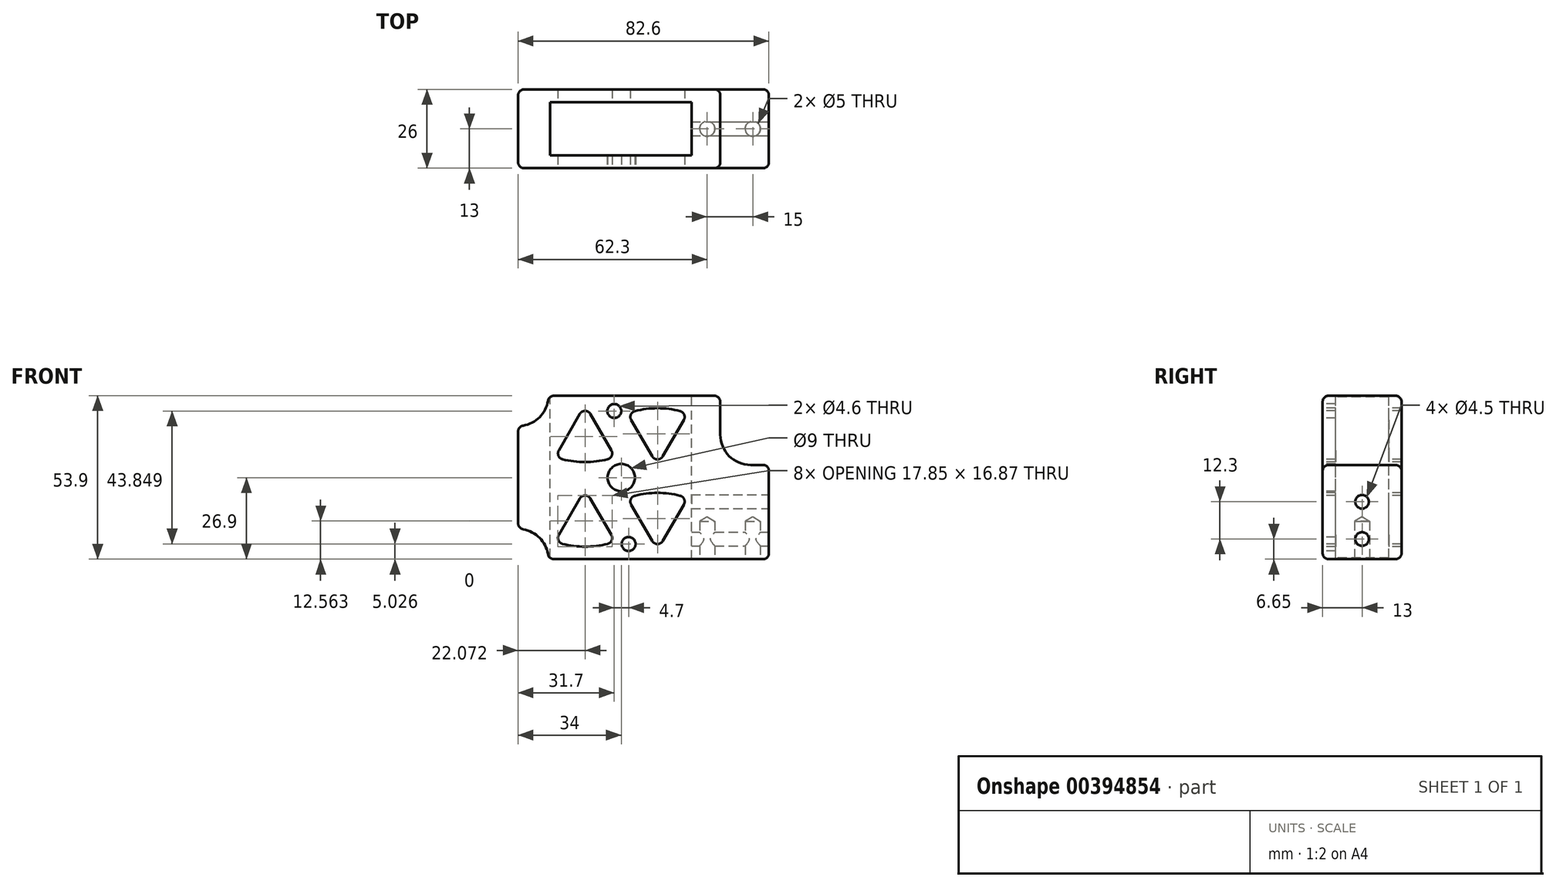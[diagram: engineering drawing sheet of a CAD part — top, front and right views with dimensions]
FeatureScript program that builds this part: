
annotation { "Feature Type Name" : "Feature", "Feature Type Description" : "" }
export const myFeature = defineFeature(function(context is Context, id is Id, definition is map)
    precondition{}
    {
        {
            var Q0;
            Q0=qCreatedBy(makeId("Front.planeOp"),FACE);
            var sketch = newSketch(context, id + "F0", { "sketchPlane" : qUnion([Q0])});
            skLineSegment(sketch, "E0.bottom", {"start": v(-29.47, 53.9) * mm, "end": v(23.3, 53.9) * mm});
            skLineSegment(sketch, "E0.top", {"start": v(-29.47, 0) * mm, "end": v(39.3, 0) * mm});
            skLineSegment(sketch, "E0.left", {"start": v(-41.3, 42.07) * mm, "end": v(-41.3, 11.83) * mm});
            skLineSegment(sketch, "E0.right", {"start": v(41.3, 29.08) * mm, "end": v(41.3, 2) * mm});
            skArc(sketch, "E1", {"start": v(-31.44, 1.67) * mm, "mid": v(-34.23, 7.07) * mm, "end": v(-39.63, 9.86) * mm});
            skArc(sketch, "E2", {"start": v(-39.63, 44.04) * mm, "mid": v(-34.23, 46.83) * mm, "end": v(-31.44, 52.23) * mm});
            skLineSegment(sketch, "E3", {"start": v(25.3, 51.9) * mm, "end": v(25.3, 41.08) * mm});
            skLineSegment(sketch, "E4", {"start": v(35.3, 31.08) * mm, "end": v(39.3, 31.08) * mm});
            skArc(sketch, "E5", {"start": v(25.3, 41.08) * mm, "mid": v(28.23, 34) * mm, "end": v(35.3, 31.08) * mm});
            skPoint(sketch, "E6.visualSharp", {"position": v(-31.3, 53.9) * mm});
            skArc(sketch, "E6.filletArc", {"start": v(-29.47, 53.9) * mm, "mid": v(-30.76, 53.43) * mm, "end": v(-31.44, 52.23) * mm});
            skPoint(sketch, "E7.visualSharp", {"position": v(-41.3, 43.9) * mm});
            skArc(sketch, "E7.filletArc", {"start": v(-39.63, 44.04) * mm, "mid": v(-40.83, 43.36) * mm, "end": v(-41.3, 42.07) * mm});
            skPoint(sketch, "E8.visualSharp", {"position": v(-41.3, 10) * mm});
            skArc(sketch, "E8.filletArc", {"start": v(-41.3, 11.83) * mm, "mid": v(-40.83, 10.54) * mm, "end": v(-39.63, 9.86) * mm});
            skPoint(sketch, "E9.visualSharp", {"position": v(-31.3, 0) * mm});
            skArc(sketch, "E9.filletArc", {"start": v(-31.44, 1.67) * mm, "mid": v(-30.76, 0.47) * mm, "end": v(-29.47, 0) * mm});
            skPoint(sketch, "E10.visualSharp", {"position": v(41.3, 0) * mm});
            skArc(sketch, "E10.filletArc", {"start": v(39.3, 0) * mm, "mid": v(40.71, 0.59) * mm, "end": v(41.3, 2) * mm});
            skPoint(sketch, "E11.orphan", {"position": v(41.3, 53.9) * mm});
            skPoint(sketch, "E12.visualSharp", {"position": v(25.3, 53.9) * mm});
            skArc(sketch, "E12.filletArc", {"start": v(25.3, 51.9) * mm, "mid": v(24.71, 53.31) * mm, "end": v(23.3, 53.9) * mm});
            skPoint(sketch, "E13.visualSharp", {"position": v(41.3, 31.08) * mm});
            skArc(sketch, "E13.filletArc", {"start": v(41.3, 29.08) * mm, "mid": v(40.71, 30.5) * mm, "end": v(39.3, 31.08) * mm});
            skSolve(sketch);
        }
        {
            var Q0;
            Q0=qSketchRegion(id+"F0",true);
            extrude(context, id + "F1", {"entities" : qUnion([Q0]), "oppositeDirection" : true, "depth" : 26 * mm});
        }
        {
            var Q0;
            Q0=makeQuery(id+"F1.opExtrude","SWEPT_FACE",FACE,{"disambiguationData":[OSD([sQuery(id+"F0.wireOp",EDGE,"E0.bottom")])]});
            var sketch = newSketch(context, id + "F2", { "sketchPlane" : qUnion([Q0])});
            skLineSegment(sketch, "E14.bottom", {"start": v(-30.72, 21.75) * mm, "end": v(15.8, 21.75) * mm});
            skLineSegment(sketch, "E14.top", {"start": v(-30.72, 4.25) * mm, "end": v(15.8, 4.25) * mm});
            skLineSegment(sketch, "E14.left", {"start": v(-30.72, 21.75) * mm, "end": v(-30.72, 4.25) * mm});
            skLineSegment(sketch, "E14.right", {"start": v(15.8, 21.75) * mm, "end": v(15.8, 4.25) * mm});
            skSolve(sketch);
        }
        {
            var Q0;
            Q0=qSketchRegion(id+"F2",true);
            extrude(context, id + "F3", {"entities" : qUnion([Q0]), "operationType" : NewBodyOperationType.REMOVE, "endBound" : BoundingType.THROUGH_ALL, "oppositeDirection" : true, "depth" : 25 * mm});
        }
        {
            var Q0;
            Q0=makeQuery(id+"F1.opExtrude","CAP_FACE",FACE,{"disambiguationData":[OSD([sQuery(id+"F0.wireOp",EDGE,"E0.bottom"),sQuery(id+"F0.wireOp",EDGE,"E0.top"),sQuery(id+"F0.wireOp",EDGE,"E0.left"),sQuery(id+"F0.wireOp",EDGE,"E0.right"),sQuery(id+"F0.wireOp",EDGE,"E1"),sQuery(id+"F0.wireOp",EDGE,"E2"),sQuery(id+"F0.wireOp",EDGE,"E3"),sQuery(id+"F0.wireOp",EDGE,"E4"),sQuery(id+"F0.wireOp",EDGE,"E5"),sQuery(id+"F0.wireOp",EDGE,"E6.filletArc"),sQuery(id+"F0.wireOp",EDGE,"E7.filletArc"),sQuery(id+"F0.wireOp",EDGE,"E8.filletArc"),sQuery(id+"F0.wireOp",EDGE,"E9.filletArc"),sQuery(id+"F0.wireOp",EDGE,"E10.filletArc"),sQuery(id+"F0.wireOp",EDGE,"E12.filletArc"),sQuery(id+"F0.wireOp",EDGE,"E13.filletArc")])],"isStart":true});
            var sketch = newSketch(context, id + "F4", { "sketchPlane" : qUnion([Q0])});
            skPoint(sketch, "E15", {"position": v(-7.3, 26.9) * mm});
            skSolve(sketch);
        }
        {
            var Q0;
            Q0=sQuery(id+"F4.wireOp",VERTEX,"E15");
            var Q1;
            Q1=makeQuery(id+"F1.opExtrude","SWEPT_BODY",BODY,{"disambiguationData":[OSD([sQuery(id+"F0.wireOp",EDGE,"E0.bottom"),sQuery(id+"F0.wireOp",EDGE,"E0.top"),sQuery(id+"F0.wireOp",EDGE,"E0.left"),sQuery(id+"F0.wireOp",EDGE,"E0.right"),sQuery(id+"F0.wireOp",EDGE,"E1"),sQuery(id+"F0.wireOp",EDGE,"E2"),sQuery(id+"F0.wireOp",EDGE,"E3"),sQuery(id+"F0.wireOp",EDGE,"E4"),sQuery(id+"F0.wireOp",EDGE,"E5"),sQuery(id+"F0.wireOp",EDGE,"E6.filletArc"),sQuery(id+"F0.wireOp",EDGE,"E7.filletArc"),sQuery(id+"F0.wireOp",EDGE,"E8.filletArc"),sQuery(id+"F0.wireOp",EDGE,"E9.filletArc"),sQuery(id+"F0.wireOp",EDGE,"E10.filletArc"),sQuery(id+"F0.wireOp",EDGE,"E12.filletArc"),sQuery(id+"F0.wireOp",EDGE,"E13.filletArc")])]});
            hole(context, id + "F5", {"style" : HoleStyle.SIMPLE, "endStyle" : HoleEndStyle.BLIND, "holeDiameter" : 9 * mm, "holeDepth" : 12 * mm, "isTappedThrough" : true, "tappedDepth" : 12 * mm, "tapClearance" : 3, "locations" : qUnion([Q0]), "scope" : qUnion([Q1])});
        }
        {
            var Q0;
            Q0=makeQuery(id+"F1.opExtrude","SWEPT_FACE",FACE,{"disambiguationData":[OSD([sQuery(id+"F0.wireOp",EDGE,"E0.right")])]});
            var sketch = newSketch(context, id + "F6", { "sketchPlane" : qUnion([Q0])});
            skPoint(sketch, "E16", {"position": v(13, 18.95) * mm});
            skPoint(sketch, "E17", {"position": v(13, 6.65) * mm});
            skSolve(sketch);
        }
        {
            var Q0;
            Q0=sQuery(id+"F6.wireOp",VERTEX,"E16");
            var Q1;
            Q1=sQuery(id+"F6.wireOp",VERTEX,"E17");
            var Q2;
            Q2=makeQuery(id+"F1.opExtrude","SWEPT_BODY",BODY,{"disambiguationData":[OSD([sQuery(id+"F0.wireOp",EDGE,"E0.bottom"),sQuery(id+"F0.wireOp",EDGE,"E0.top"),sQuery(id+"F0.wireOp",EDGE,"E0.left"),sQuery(id+"F0.wireOp",EDGE,"E0.right"),sQuery(id+"F0.wireOp",EDGE,"E1"),sQuery(id+"F0.wireOp",EDGE,"E2"),sQuery(id+"F0.wireOp",EDGE,"E3"),sQuery(id+"F0.wireOp",EDGE,"E4"),sQuery(id+"F0.wireOp",EDGE,"E5"),sQuery(id+"F0.wireOp",EDGE,"E6.filletArc"),sQuery(id+"F0.wireOp",EDGE,"E7.filletArc"),sQuery(id+"F0.wireOp",EDGE,"E8.filletArc"),sQuery(id+"F0.wireOp",EDGE,"E9.filletArc"),sQuery(id+"F0.wireOp",EDGE,"E10.filletArc"),sQuery(id+"F0.wireOp",EDGE,"E12.filletArc"),sQuery(id+"F0.wireOp",EDGE,"E13.filletArc")])]});
            hole(context, id + "F7", {"style" : HoleStyle.SIMPLE, "endStyle" : HoleEndStyle.BLIND, "holeDiameter" : 4.5 * mm, "holeDepth" : 30 * mm, "isTappedThrough" : true, "tappedDepth" : 27.9 * mm, "tapClearance" : 3, "locations" : qUnion([Q0, Q1]), "scope" : qUnion([Q2])});
        }
        {
            var Q0;
            Q0=makeQuery(id+"F1.opExtrude","SWEPT_FACE",FACE,{"disambiguationData":[OSD([sQuery(id+"F0.wireOp",EDGE,"E0.top")])]});
            var sketch = newSketch(context, id + "F8", { "sketchPlane" : qUnion([Q0])});
            skPoint(sketch, "E18", {"position": v(36, -13) * mm});
            skPoint(sketch, "E18.positionSnap0", {"position": v(39.3, -13) * mm});
            skPoint(sketch, "E19", {"position": v(21, -13) * mm});
            skSolve(sketch);
        }
        {
            var Q0;
            Q0=sQuery(id+"F8.wireOp",VERTEX,"E18");
            var Q1;
            Q1=sQuery(id+"F8.wireOp",VERTEX,"E19");
            var Q2;
            Q2=makeQuery(id+"F1.opExtrude","SWEPT_BODY",BODY,{"disambiguationData":[OSD([sQuery(id+"F0.wireOp",EDGE,"E0.bottom"),sQuery(id+"F0.wireOp",EDGE,"E0.top"),sQuery(id+"F0.wireOp",EDGE,"E0.left"),sQuery(id+"F0.wireOp",EDGE,"E0.right"),sQuery(id+"F0.wireOp",EDGE,"E1"),sQuery(id+"F0.wireOp",EDGE,"E2"),sQuery(id+"F0.wireOp",EDGE,"E3"),sQuery(id+"F0.wireOp",EDGE,"E4"),sQuery(id+"F0.wireOp",EDGE,"E5"),sQuery(id+"F0.wireOp",EDGE,"E6.filletArc"),sQuery(id+"F0.wireOp",EDGE,"E7.filletArc"),sQuery(id+"F0.wireOp",EDGE,"E8.filletArc"),sQuery(id+"F0.wireOp",EDGE,"E9.filletArc"),sQuery(id+"F0.wireOp",EDGE,"E10.filletArc"),sQuery(id+"F0.wireOp",EDGE,"E12.filletArc"),sQuery(id+"F0.wireOp",EDGE,"E13.filletArc")])]});
            hole(context, id + "F9", {"style" : HoleStyle.SIMPLE, "endStyle" : HoleEndStyle.BLIND, "standardTappedOrClearance" : lookupTablePath({ "standard" : "ISO", "engagement" : "75%", "pitch" : "1 mm", "size" : "M6", "type" : "Tapped" }), "standardBlindInLast" : lookupTablePath({ "standard" : "ISO", "engagement" : "75%", "pitch" : "1 mm", "size" : "M6", "type" : "Tapped" }), "holeDiameter" : 5 * mm, "showTappedDepth" : true, "holeDepth" : 12.5 * mm, "isTappedThrough" : true, "tappedDepth" : 9.5 * mm, "tapClearance" : 3, "locations" : qUnion([Q0, Q1]), "scope" : qUnion([Q2]), "majorDiameter" : 6 * mm});
        }
        {
            var Q0;
            Q0=makeQuery(id+"F1.opExtrude","CAP_FACE",FACE,{"disambiguationData":[OSD([sQuery(id+"F0.wireOp",EDGE,"E0.bottom"),sQuery(id+"F0.wireOp",EDGE,"E0.top"),sQuery(id+"F0.wireOp",EDGE,"E0.left"),sQuery(id+"F0.wireOp",EDGE,"E0.right"),sQuery(id+"F0.wireOp",EDGE,"E1"),sQuery(id+"F0.wireOp",EDGE,"E2"),sQuery(id+"F0.wireOp",EDGE,"E3"),sQuery(id+"F0.wireOp",EDGE,"E4"),sQuery(id+"F0.wireOp",EDGE,"E5"),sQuery(id+"F0.wireOp",EDGE,"E6.filletArc"),sQuery(id+"F0.wireOp",EDGE,"E7.filletArc"),sQuery(id+"F0.wireOp",EDGE,"E8.filletArc"),sQuery(id+"F0.wireOp",EDGE,"E9.filletArc"),sQuery(id+"F0.wireOp",EDGE,"E10.filletArc"),sQuery(id+"F0.wireOp",EDGE,"E12.filletArc"),sQuery(id+"F0.wireOp",EDGE,"E13.filletArc")])],"isStart":true});
            var sketch = newSketch(context, id + "F10", { "sketchPlane" : qUnion([Q0])});
            skCircle(sketch, "E20", {"center": v(-9.6, 48.87) * mm, "radius": 2.3 * mm});
            skCircle(sketch, "E21", {"center": v(-4.9, 5.03) * mm, "radius": 2.3 * mm});
            skLineSegment(sketch, "E22", {"start": v(-66.21, 51.17) * mm, "end": v(48.12, 51.17) * mm, "construction": true});
            skLineSegment(sketch, "E23", {"start": v(-60.61, 2.73) * mm, "end": v(50.15, 2.73) * mm, "construction": true});
            skLineSegment(sketch, "E24", {"start": v(-9.6, 48.87) * mm, "end": v(-9.6, 53.9) * mm, "construction": true});
            skLineSegment(sketch, "E25", {"start": v(-4.9, 5.03) * mm, "end": v(-4.9, 0) * mm, "construction": true});
            skSolve(sketch);
        }
        {
            var Q0;
            Q0=sQuery(id+"F10.wireOp",VERTEX,"E20.center");
            var Q1;
            Q1=sQuery(id+"F10.wireOp",VERTEX,"E25.start");
            var Q2;
            Q2=makeQuery(id+"F1.opExtrude","SWEPT_BODY",BODY,{"disambiguationData":[OSD([sQuery(id+"F0.wireOp",EDGE,"E0.bottom"),sQuery(id+"F0.wireOp",EDGE,"E0.top"),sQuery(id+"F0.wireOp",EDGE,"E0.left"),sQuery(id+"F0.wireOp",EDGE,"E0.right"),sQuery(id+"F0.wireOp",EDGE,"E1"),sQuery(id+"F0.wireOp",EDGE,"E2"),sQuery(id+"F0.wireOp",EDGE,"E3"),sQuery(id+"F0.wireOp",EDGE,"E4"),sQuery(id+"F0.wireOp",EDGE,"E5"),sQuery(id+"F0.wireOp",EDGE,"E6.filletArc"),sQuery(id+"F0.wireOp",EDGE,"E7.filletArc"),sQuery(id+"F0.wireOp",EDGE,"E8.filletArc"),sQuery(id+"F0.wireOp",EDGE,"E9.filletArc"),sQuery(id+"F0.wireOp",EDGE,"E10.filletArc"),sQuery(id+"F0.wireOp",EDGE,"E12.filletArc"),sQuery(id+"F0.wireOp",EDGE,"E13.filletArc")])]});
            hole(context, id + "F11", {"style" : HoleStyle.SIMPLE, "endStyle" : HoleEndStyle.BLIND, "holeDiameter" : 4.6 * mm, "holeDepth" : 12.5 * mm, "isTappedThrough" : true, "tappedDepth" : 9.5 * mm, "tapClearance" : 3, "locations" : qUnion([Q0, Q1]), "scope" : qUnion([Q2])});
        }
        {
            var Q0;
            Q0=makeQuery(id+"F1.opExtrude","CAP_FACE",FACE,{"disambiguationData":[OSD([sQuery(id+"F0.wireOp",EDGE,"E0.bottom"),sQuery(id+"F0.wireOp",EDGE,"E0.top"),sQuery(id+"F0.wireOp",EDGE,"E0.left"),sQuery(id+"F0.wireOp",EDGE,"E0.right"),sQuery(id+"F0.wireOp",EDGE,"E1"),sQuery(id+"F0.wireOp",EDGE,"E2"),sQuery(id+"F0.wireOp",EDGE,"E3"),sQuery(id+"F0.wireOp",EDGE,"E4"),sQuery(id+"F0.wireOp",EDGE,"E5"),sQuery(id+"F0.wireOp",EDGE,"E6.filletArc"),sQuery(id+"F0.wireOp",EDGE,"E7.filletArc"),sQuery(id+"F0.wireOp",EDGE,"E8.filletArc"),sQuery(id+"F0.wireOp",EDGE,"E9.filletArc"),sQuery(id+"F0.wireOp",EDGE,"E10.filletArc"),sQuery(id+"F0.wireOp",EDGE,"E12.filletArc"),sQuery(id+"F0.wireOp",EDGE,"E13.filletArc")])],"isStart":true});
            var sketch = newSketch(context, id + "F12", { "sketchPlane" : qUnion([Q0])});
            skLineSegment(sketch, "E26", {"start": v(-17.5, 47.9) * mm, "end": v(-10.57, 35.9) * mm});
            skLineSegment(sketch, "E27", {"start": v(-12.3, 32.9) * mm, "end": v(-26.16, 32.9) * mm});
            skLineSegment(sketch, "E28", {"start": v(-27.89, 35.9) * mm, "end": v(-20.96, 47.9) * mm});
            skPoint(sketch, "E29.visualSharp", {"position": v(-19.23, 50.9) * mm});
            skArc(sketch, "E29.filletArc", {"start": v(-17.5, 47.9) * mm, "mid": v(-19.23, 48.9) * mm, "end": v(-20.96, 47.9) * mm});
            skArc(sketch, "E30.filletArc", {"start": v(-12.3, 32.9) * mm, "mid": v(-10.57, 33.9) * mm, "end": v(-10.57, 35.9) * mm});
            skPoint(sketch, "E31.visualSharp", {"position": v(-29.62, 32.9) * mm});
            skArc(sketch, "E31.filletArc", {"start": v(-27.89, 35.9) * mm, "mid": v(-27.89, 33.9) * mm, "end": v(-26.16, 32.9) * mm});
            skLineSegment(sketch, "E32", {"start": v(-7.3, 59.95) * mm, "end": v(-7.3, -3) * mm, "construction": true});
            skLineSegment(sketch, "E33", {"start": v(-48.51, 26.9) * mm, "end": v(45.71, 26.9) * mm, "construction": true});
            skLineSegment(sketch, "E34", {"start": v(-30.72, 56.6) * mm, "end": v(-30.72, -1.77) * mm, "construction": true});
            skLineSegment(sketch, "E35", {"start": v(-2.3, 48.9) * mm, "end": v(11.56, 48.9) * mm});
            skLineSegment(sketch, "E36", {"start": v(13.29, 45.9) * mm, "end": v(6.36, 33.9) * mm});
            skLineSegment(sketch, "E37", {"start": v(2.9, 33.9) * mm, "end": v(-4.03, 45.9) * mm});
            skPoint(sketch, "E38.visualSharp", {"position": v(4.63, 30.9) * mm});
            skArc(sketch, "E38.filletArc", {"start": v(2.9, 33.9) * mm, "mid": v(4.63, 32.9) * mm, "end": v(6.36, 33.9) * mm});
            skPoint(sketch, "E39.visualSharp", {"position": v(15.02, 48.9) * mm});
            skArc(sketch, "E39.filletArc", {"start": v(13.29, 45.9) * mm, "mid": v(13.29, 47.9) * mm, "end": v(11.56, 48.9) * mm});
            skPoint(sketch, "E40.visualSharp", {"position": v(-5.76, 48.9) * mm});
            skArc(sketch, "E40.filletArc", {"start": v(-2.3, 48.9) * mm, "mid": v(-4.03, 47.9) * mm, "end": v(-4.03, 45.9) * mm});
            skLineSegment(sketch, "E41", {"start": v(-27.89, 8) * mm, "end": v(-20.96, 20) * mm});
            skLineSegment(sketch, "E42", {"start": v(-17.5, 20) * mm, "end": v(-10.57, 8) * mm});
            skLineSegment(sketch, "E43", {"start": v(-12.3, 5) * mm, "end": v(-26.16, 5) * mm});
            skPoint(sketch, "E44.visualSharp", {"position": v(-19.23, 23) * mm});
            skArc(sketch, "E44.filletArc", {"start": v(-17.5, 20) * mm, "mid": v(-19.23, 21) * mm, "end": v(-20.96, 20) * mm});
            skPoint(sketch, "E45.visualSharp", {"position": v(-8.84, 5) * mm});
            skArc(sketch, "E45.filletArc", {"start": v(-12.3, 5) * mm, "mid": v(-10.57, 6) * mm, "end": v(-10.57, 8) * mm});
            skPoint(sketch, "E46.visualSharp", {"position": v(-29.62, 5) * mm});
            skArc(sketch, "E46.filletArc", {"start": v(-27.89, 8) * mm, "mid": v(-27.89, 6) * mm, "end": v(-26.16, 5) * mm});
            skLineSegment(sketch, "E47", {"start": v(-4.03, 18) * mm, "end": v(2.9, 6) * mm});
            skLineSegment(sketch, "E48", {"start": v(6.36, 6) * mm, "end": v(13.29, 18) * mm});
            skLineSegment(sketch, "E49", {"start": v(11.56, 21) * mm, "end": v(-2.3, 21) * mm});
            skPoint(sketch, "E50.visualSharp", {"position": v(-5.76, 21) * mm});
            skArc(sketch, "E50.filletArc", {"start": v(-2.3, 21) * mm, "mid": v(-4.03, 20) * mm, "end": v(-4.03, 18) * mm});
            skPoint(sketch, "E51.visualSharp", {"position": v(4.63, 3) * mm});
            skArc(sketch, "E51.filletArc", {"start": v(2.9, 6) * mm, "mid": v(4.63, 5) * mm, "end": v(6.36, 6) * mm});
            skPoint(sketch, "E52.visualSharp", {"position": v(15.02, 21) * mm});
            skArc(sketch, "E52.filletArc", {"start": v(13.29, 18) * mm, "mid": v(13.29, 20) * mm, "end": v(11.56, 21) * mm});
            skArc(sketch, "E53", {"start": v(-26.65, 32.96) * mm, "mid": v(-19.23, 32.03) * mm, "end": v(-11.8, 32.96) * mm});
            skArc(sketch, "E54", {"start": v(-26.65, 5.06) * mm, "mid": v(-19.23, 4.13) * mm, "end": v(-11.8, 5.06) * mm});
            skArc(sketch, "E55", {"start": v(12.05, 20.94) * mm, "mid": v(4.63, 21.87) * mm, "end": v(-2.8, 20.94) * mm});
            skArc(sketch, "E56", {"start": v(12.05, 48.84) * mm, "mid": v(4.63, 49.77) * mm, "end": v(-2.8, 48.84) * mm});
            skSolve(sketch);
        }
        {
            var Q0;
            Q0=qSketchRegion(id+"F12",true);
            extrude(context, id + "F13", {"entities" : qUnion([Q0]), "operationType" : NewBodyOperationType.REMOVE, "endBound" : BoundingType.THROUGH_ALL, "oppositeDirection" : true, "depth" : 25 * mm});
        }
        {
            var Q0;
            Q0=makeQuery(id+"F1.opExtrude","SWEPT_FACE",FACE,{"disambiguationData":[OSD([sQuery(id+"F0.wireOp",EDGE,"E0.left")])]});
            fillet(context, id + "F14", {"entities" : qUnion([Q0]), "radius" : 2 * mm, "tangentPropagation" : true, "allowEdgeOverflow" : false});
        }
    });
